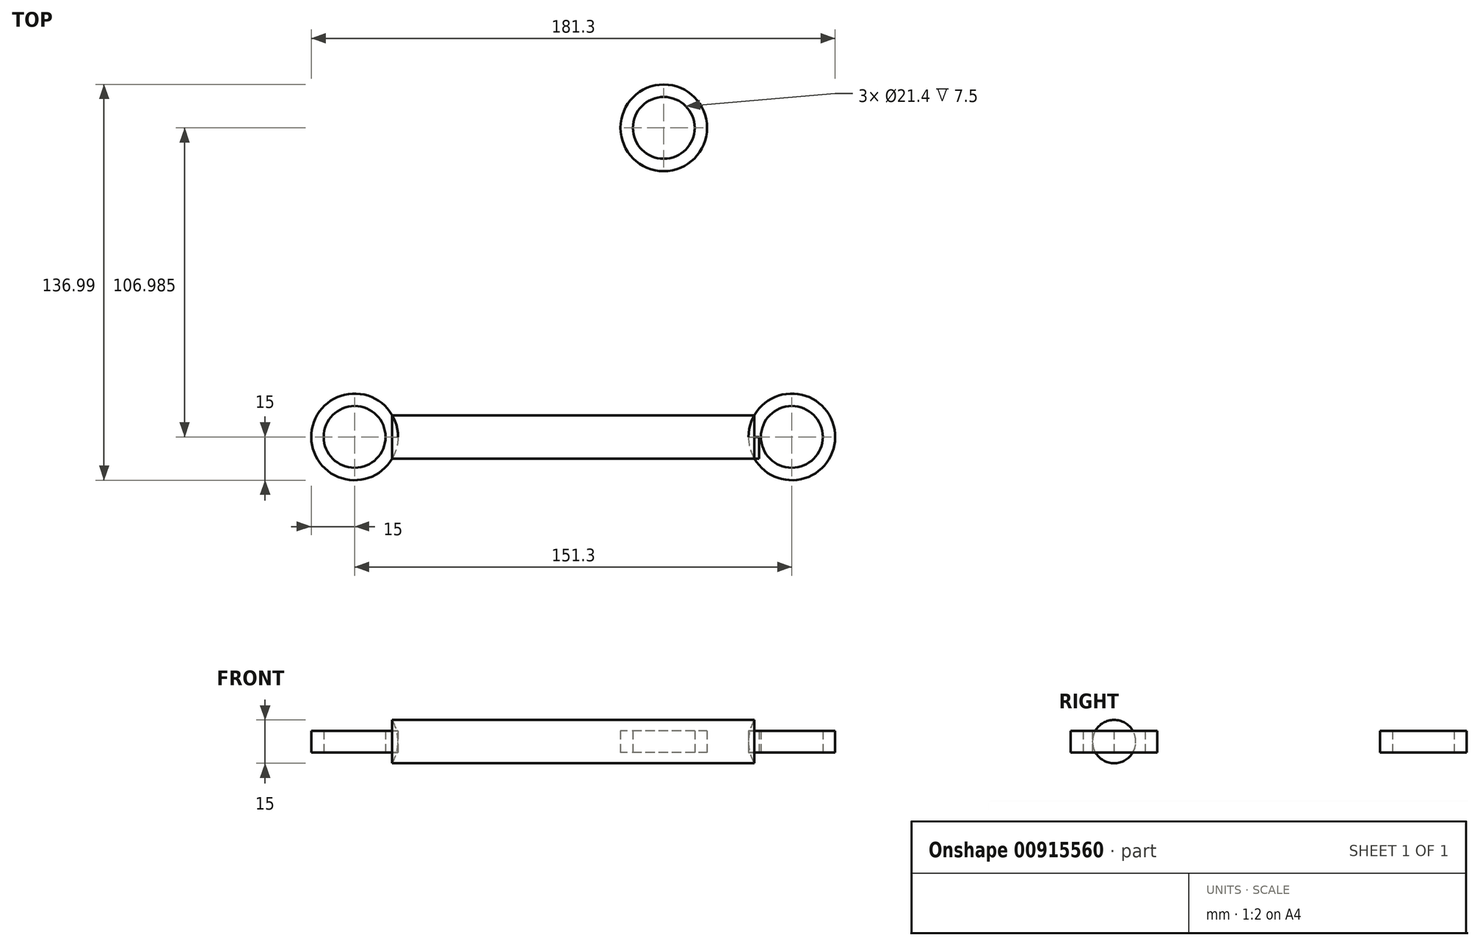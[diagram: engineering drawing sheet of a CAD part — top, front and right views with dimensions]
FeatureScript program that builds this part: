
annotation { "Feature Type Name" : "Feature", "Feature Type Description" : "" }
export const myFeature = defineFeature(function(context is Context, id is Id, definition is map)
    precondition{}
    {
        {
            var Q0;
            Q0=qCreatedBy(makeId("Top.planeOp"),FACE);
            var sketch = newSketch(context, id + "F0", { "sketchPlane" : qUnion([Q0])});
            skCircle(sketch, "E0", {"center": v(0, 0) * mm, "radius": 10.7 * mm});
            skCircle(sketch, "E1", {"center": v(0, 0) * mm, "radius": 15 * mm});
            skLineSegment(sketch, "E2.left", {"start": v(104.3, 93.7) * mm, "end": v(18.1, 7.5) * mm});
            skLineSegment(sketch, "E2.right", {"start": v(93.7, 104.3) * mm, "end": v(3.88, 14.49) * mm});
            skLineSegment(sketch, "E3.bottom", {"start": v(140, -7.5) * mm, "end": v(13, -7.5) * mm});
            skLineSegment(sketch, "E3.top", {"start": v(140, 7.5) * mm, "end": v(18.1, 7.5) * mm});
            skPoint(sketch, "E2.top.end.orphan", {"position": v(-104.3, -93.7) * mm});
            skPoint(sketch, "E2.top.start.orphan", {"position": v(-93.7, -104.3) * mm});
            skPoint(sketch, "E3.right.end.orphan", {"position": v(-140, 7.5) * mm});
            skPoint(sketch, "E3.right.start.orphan", {"position": v(-140, -7.5) * mm});
            skCircle(sketch, "E4", {"center": v(151.3, 0) * mm, "radius": 10.7 * mm});
            skCircle(sketch, "E5", {"center": v(151.3, 0) * mm, "radius": 15 * mm});
            skCircle(sketch, "E6", {"center": v(106.99, 106.99) * mm, "radius": 10.7 * mm});
            skCircle(sketch, "E7", {"center": v(106.99, 106.99) * mm, "radius": 15 * mm});
            skLineSegment(sketch, "E8", {"start": v(0, 0) * mm, "end": v(106.99, 106.99) * mm, "construction": true});
            skLineSegment(sketch, "E9.bottom", {"start": v(13, -7.5) * mm, "end": v(139.99, -7.5) * mm});
            skLineSegment(sketch, "E9.top", {"start": v(13, 0) * mm, "end": v(139.99, 0) * mm});
            skLineSegment(sketch, "E9.left", {"start": v(13, -7.5) * mm, "end": v(13, 0) * mm});
            skLineSegment(sketch, "E9.right", {"start": v(139.99, -7.5) * mm, "end": v(139.99, 0) * mm});
            skSolve(sketch);
        }
        {
            var Q0;
            Q0=makeQuery(id+"F0.imprint","IMPRINT",FACE,{"disambiguationData":[TD([[makeQuery(id+"F0.imprint","IMPRINT",EDGE,{"derivedFrom":sQuery(id+"F0.wireOp",EDGE,"E0")}),-1.0]])]});
            var Q1;
            Q1=makeQuery(id+"F0.imprint","IMPRINT",FACE,{"disambiguationData":[TD([[makeQuery(id+"F0.imprint","IMPRINT",EDGE,{"derivedFrom":sQuery(id+"F0.wireOp",EDGE,"E4")}),-1.0]])]});
            var Q2;
            Q2=makeQuery(id+"F0.imprint","IMPRINT",FACE,{"disambiguationData":[TD([[makeQuery(id+"F0.imprint","IMPRINT",EDGE,{"derivedFrom":sQuery(id+"F0.wireOp",EDGE,"E6")}),-1.0]])]});
            extrude(context, id + "F1", {"entities" : qUnion([Q0, Q1, Q2]), "endBound" : BoundingType.SYMMETRIC, "depth" : 7.5 * mm, "offsetDistance" : 25 * mm});
        }
        {
            var Q0;
            {var subQ0=sQuery(id+"F0.wireOp",EDGE,"E9.bottom");var subQ5=sQuery(id+"F0.wireOp",EDGE,"E5");var subQ6=makeQuery(id+"F0.imprint","INTERSECT",VERTEX,{"derivedFrom":[subQ5,subQ0]});Q0=makeQuery(id+"F0.imprint","IMPRINT",FACE,{"disambiguationData":[TD([[makeQuery(id+"F0.imprint","IMPRINT",EDGE,{"disambiguationData":[TD([[subQ6,1.0]])],"derivedFrom":subQ5}),-1.0]])]});}
            var Q1;
            Q1=sQuery(id+"F0.wireOp",EDGE,"E9.top");
            revolve(context, id + "F2", {"surfaceOperationType" : NewSurfaceOperationType.NEW, "entities" : qUnion([Q0]), "axis" : qUnion([Q1]), "revolveType" : RevolveType.FULL});
        }
    });
